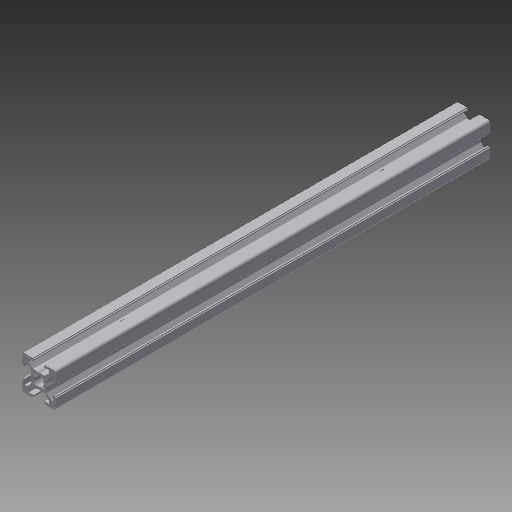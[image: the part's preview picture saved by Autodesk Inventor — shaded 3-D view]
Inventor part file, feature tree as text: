
AUTODESK INVENTOR PART (.ipt)
format: ipt  version: 2019 (Build 230136000, 136)  size: 404,992 bytes
history: native  units: in
note: dims shown in document units (in); Inventor stores cm internally (conversion verified against a paired STEP export)
features: other x3, sketch x2, extrude x1, hole x1, mirror x1
ambient origin geometry x8: Origin, YZ Plane, XZ Plane, XY Plane, X Axis, Y Axis, Z Axis, Center Point
bodies: Solid1 (feature_tree)
feature tree (8):
  other  "Blocks"
  extrude  "Extrusion1"  Depth=2.0in
  hole  "Hole1"  [1 undecoded]
  mirror  "Mirror1"
  sketch  "Sketch1"  dims[d1=0.0in d5=2.0in]
  other  "20x20"
  sketch  "Sketch3"  dims[d6=0.187in d7=0.75in d8=0.375in d9=0.25in d10=0.5635in d11=1.0in d12=0.8108in d13=1.0in d14=1.0in]
  other  "20x20:1"
note: 1 required parameter value undecoded (feature->parameter linkage not recoverable at this tier; creation-order binding heuristic only, values carry confidence <= 0.55)
